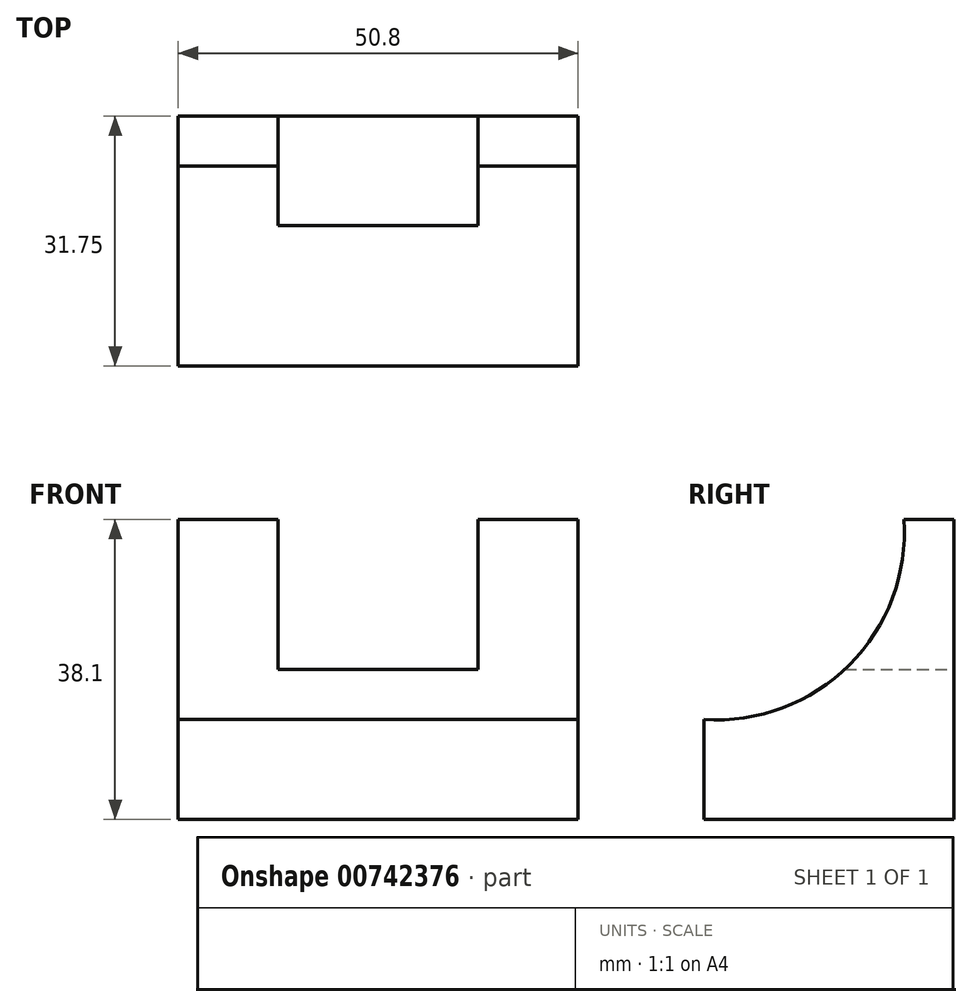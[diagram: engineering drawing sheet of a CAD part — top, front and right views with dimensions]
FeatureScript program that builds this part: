
annotation { "Feature Type Name" : "Feature", "Feature Type Description" : "" }
export const myFeature = defineFeature(function(context is Context, id is Id, definition is map)
    precondition{}
    {
        {
            var Q0;
            Q0=qCreatedBy(makeId("Front.planeOp"),FACE);
            var sketch = newSketch(context, id + "F0", { "sketchPlane" : qUnion([Q0])});
            skLineSegment(sketch, "E0.bottom", {"start": v(0, 0) * mm, "end": v(-50.8, 0) * mm});
            skLineSegment(sketch, "E0.top", {"start": v(0, 38.1) * mm, "end": v(-50.8, 38.1) * mm});
            skLineSegment(sketch, "E0.left", {"start": v(0, 0) * mm, "end": v(0, 38.1) * mm});
            skLineSegment(sketch, "E0.right", {"start": v(-50.8, 0) * mm, "end": v(-50.8, 38.1) * mm});
            skSolve(sketch);
        }
        {
            var Q0;
            Q0=makeQuery(id+"F0.imprint","IMPRINT",FACE,{"disambiguationData":[TD([[makeQuery(id+"F0.imprint","IMPRINT",EDGE,{"derivedFrom":sQuery(id+"F0.wireOp",EDGE,"E0.bottom")}),-1.0]])]});
            extrude(context, id + "F1", {"entities" : qUnion([Q0]), "depth" : 31.75 * mm, "offsetDistance" : 25.4 * mm});
        }
        {
            var Q0;
            Q0=makeQuery(id+"F1.opExtrude","SWEPT_FACE",FACE,{"disambiguationData":[OSD([sQuery(id+"F0.wireOp",EDGE,"E0.left")])]});
            var sketch = newSketch(context, id + "F2", { "sketchPlane" : qUnion([Q0])});
            skArc(sketch, "E1", {"start": v(-31.75, 12.7) * mm, "mid": v(-13.29, 19.64) * mm, "end": v(-6.35, 38.1) * mm});
            skSolve(sketch);
        }
        {
            var Q0;
            {var subQ0=sQuery(id+"F2.wireOp",EDGE,"E1");Q0=makeQuery(id+"F2.imprint","IMPRINT",FACE,{"disambiguationData":[TD([[makeQuery(id+"F2.imprint","IMPRINT",EDGE,{"derivedFrom":subQ0}),1.0]])]});}
            extrude(context, id + "F3", {"entities" : qUnion([Q0]), "operationType" : NewBodyOperationType.REMOVE, "endBound" : BoundingType.THROUGH_ALL, "oppositeDirection" : true, "depth" : 25.4 * mm, "offsetDistance" : 25.4 * mm});
        }
        {
            var Q0;
            Q0=makeQuery(id+"F1.opExtrude","CAP_FACE",FACE,{"disambiguationData":[OSD([sQuery(id+"F0.wireOp",EDGE,"E0.bottom"),sQuery(id+"F0.wireOp",EDGE,"E0.top"),sQuery(id+"F0.wireOp",EDGE,"E0.left"),sQuery(id+"F0.wireOp",EDGE,"E0.right")])],"isStart":true});
            var sketch = newSketch(context, id + "F4", { "sketchPlane" : qUnion([Q0])});
            skLineSegment(sketch, "E2", {"start": v(12.7, 38.1) * mm, "end": v(12.7, 19.05) * mm});
            skLineSegment(sketch, "E3", {"start": v(12.7, 19.05) * mm, "end": v(38.1, 19.05) * mm});
            skLineSegment(sketch, "E4", {"start": v(38.1, 19.05) * mm, "end": v(38.1, 38.1) * mm});
            skLineSegment(sketch, "E5", {"start": v(38.1, 38.1) * mm, "end": v(12.7, 38.1) * mm});
            skSolve(sketch);
        }
        {
            var Q0;
            Q0=makeQuery(id+"F4.imprint","IMPRINT",FACE,{"disambiguationData":[TD([[makeQuery(id+"F4.imprint","IMPRINT",EDGE,{"derivedFrom":sQuery(id+"F4.wireOp",EDGE,"E2")}),1.0]])]});
            extrude(context, id + "F5", {"entities" : qUnion([Q0]), "operationType" : NewBodyOperationType.REMOVE, "endBound" : BoundingType.THROUGH_ALL, "oppositeDirection" : true, "depth" : 25.4 * mm, "offsetDistance" : 25.4 * mm});
        }
    });
